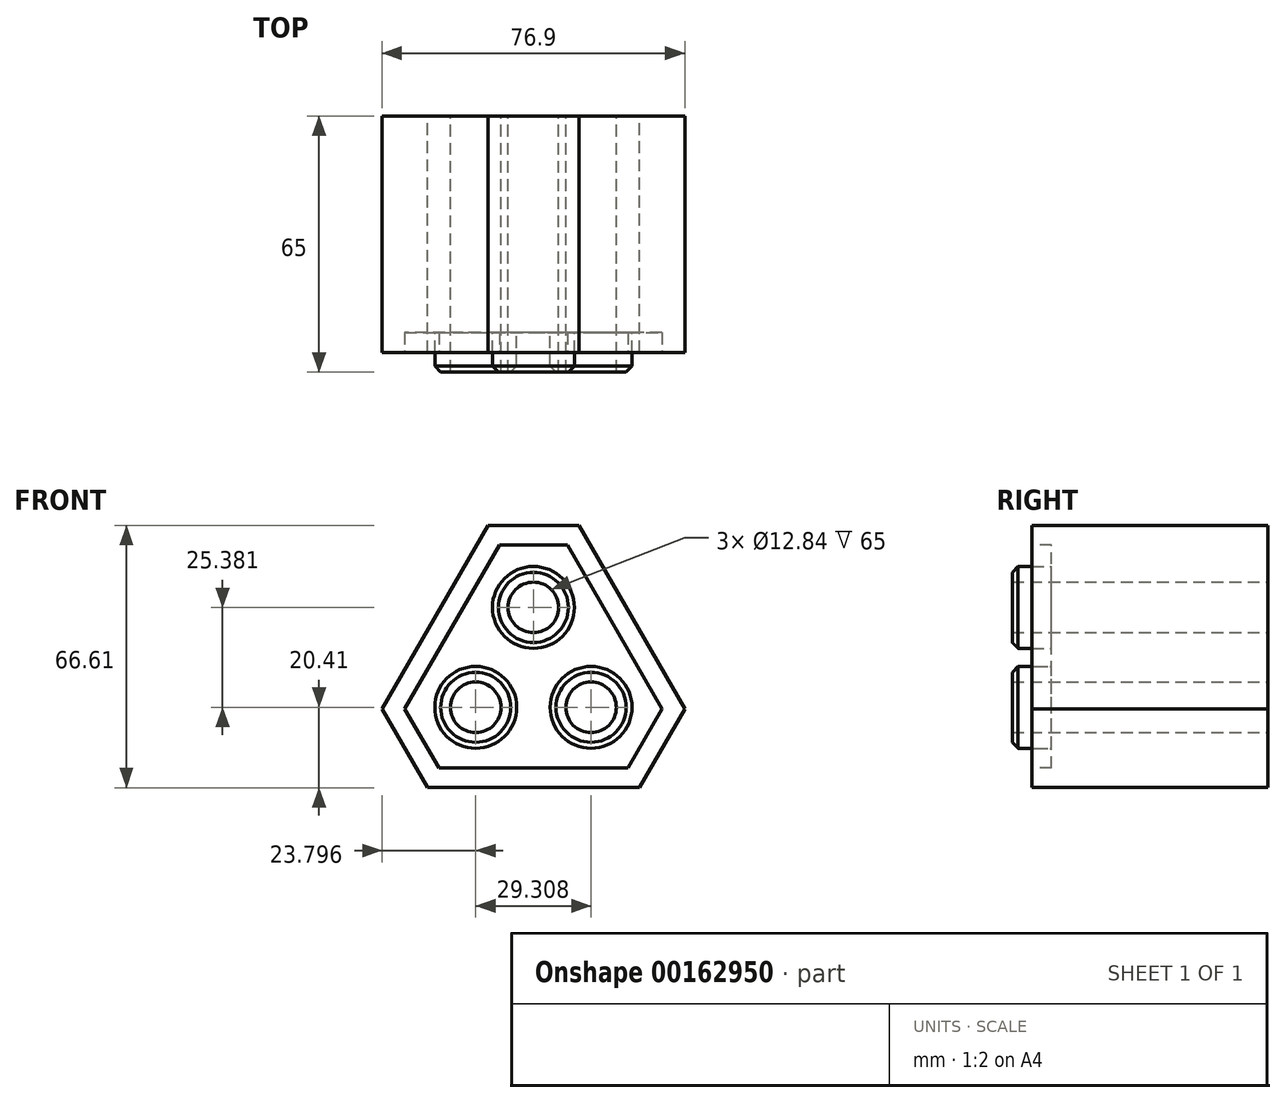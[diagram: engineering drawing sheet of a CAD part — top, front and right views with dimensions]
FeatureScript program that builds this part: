
annotation { "Feature Type Name" : "Feature", "Feature Type Description" : "" }
export const myFeature = defineFeature(function(context is Context, id is Id, definition is map)
    precondition{}
    {
        {
            assignVariable(context, id + "F0", {"name" : "loop", "anyValue" : 60});
        }
        {
            var Q0;
            Q0=qCreatedBy(makeId("Front.planeOp"),FACE);
            var sketch = newSketch(context, id + "F1", { "sketchPlane" : qUnion([Q0])});
            skCircle(sketch, "E0.cCircle", {"center": v(0, 0) * mm, "radius": 28.87 * mm, "construction": true});
            skLineSegment(sketch, "E0.0", {"start": v(50, -28.87) * mm, "end": v(-50, -28.87) * mm});
            skLineSegment(sketch, "E0.1", {"start": v(-50, -28.87) * mm, "end": v(0, 57.74) * mm});
            skLineSegment(sketch, "E0.2", {"start": v(0, 57.74) * mm, "end": v(50, -28.87) * mm});
            skPoint(sketch, "E0.0.midPoint", {"position": v(0, -28.87) * mm});
            skLineSegment(sketch, "E1", {"start": v(-11.55, 37.74) * mm, "end": v(11.55, 37.74) * mm});
            skLineSegment(sketch, "E2.1.0", {"start": v(-26.9, -28.87) * mm, "end": v(-38.45, -8.87) * mm});
            skLineSegment(sketch, "E2.2.0", {"start": v(38.45, -8.87) * mm, "end": v(26.9, -28.87) * mm});
            skSolve(sketch);
        }
        {
            var Q0;
            {var subQ0=sQuery(id+"F1.wireOp",EDGE,"E1");Q0=makeQuery(id+"F1.imprint","IMPRINT",FACE,{"disambiguationData":[TD([[makeQuery(id+"F1.imprint","IMPRINT",EDGE,{"derivedFrom":subQ0}),-1.0]])]});}
            extrude(context, id + "F2", {"entities" : qUnion([Q0]), "depth" : (getVariable(context, 'loop')) * mm, "offsetDistance" : 25 * mm});
        }
        {
            var Q0;
            Q0=makeQuery(id+"F2.opExtrude","CAP_FACE",FACE,{"disambiguationData":[OSD([sQuery(id+"F1.wireOp",EDGE,"E0.0"),sQuery(id+"F1.wireOp",EDGE,"E0.1"),sQuery(id+"F1.wireOp",EDGE,"E0.2"),sQuery(id+"F1.wireOp",EDGE,"E1"),sQuery(id+"F1.wireOp",EDGE,"E2.1.0"),sQuery(id+"F1.wireOp",EDGE,"E2.2.0")])],"isStart":false});
            var sketch = newSketch(context, id + "F3", { "sketchPlane" : qUnion([Q0])});
            skLineSegment(sketch, "E3.0", {"start": v(-24.02, -23.87) * mm, "end": v(24.02, -23.87) * mm});
            skLineSegment(sketch, "E3.1", {"start": v(32.68, -8.87) * mm, "end": v(8.66, 32.74) * mm});
            skLineSegment(sketch, "E3.2", {"start": v(8.66, 32.74) * mm, "end": v(-8.66, 32.74) * mm});
            skLineSegment(sketch, "E3.3", {"start": v(24.02, -23.87) * mm, "end": v(32.68, -8.87) * mm});
            skLineSegment(sketch, "E3.4", {"start": v(-8.66, 32.74) * mm, "end": v(-32.68, -8.87) * mm});
            skLineSegment(sketch, "E3.5", {"start": v(-32.68, -8.87) * mm, "end": v(-24.02, -23.87) * mm});
            skSolve(sketch);
        }
        {
            var Q0;
            Q0=makeQuery(id+"F3.imprint","IMPRINT",FACE,{"disambiguationData":[TD([[makeQuery(id+"F3.imprint","IMPRINT",EDGE,{"derivedFrom":sQuery(id+"F3.wireOp",EDGE,"E3.0")}),1.0]])]});
            extrude(context, id + "F4", {"entities" : qUnion([Q0]), "operationType" : NewBodyOperationType.REMOVE, "oppositeDirection" : true, "depth" : 5 * mm, "offsetDistance" : 25 * mm});
        }
        {
            var Q0;
            Q0=makeQuery(id+"F4.boolean.opBoolean","COPY",FACE,{"derivedFrom":makeQuery(id+"F4.opExtrude","CAP_FACE",FACE,{"disambiguationData":[OSD([sQuery(id+"F3.wireOp",EDGE,"E3.0"),sQuery(id+"F3.wireOp",EDGE,"E3.1"),sQuery(id+"F3.wireOp",EDGE,"E3.2"),sQuery(id+"F3.wireOp",EDGE,"E3.3"),sQuery(id+"F3.wireOp",EDGE,"E3.4"),sQuery(id+"F3.wireOp",EDGE,"E3.5")])],"isStart":false})});
            var sketch = newSketch(context, id + "F5", { "sketchPlane" : qUnion([Q0])});
            skCircle(sketch, "E4", {"center": v(0, 16.92) * mm, "radius": 10.4 * mm});
            skCircle(sketch, "E5", {"center": v(0, 16.92) * mm, "radius": 6.42 * mm});
            skCircle(sketch, "E6.1.0", {"center": v(-14.65, -8.46) * mm, "radius": 10.4 * mm});
            skCircle(sketch, "E6.1.1", {"center": v(-14.65, -8.46) * mm, "radius": 6.42 * mm});
            skCircle(sketch, "E6.2.0", {"center": v(14.65, -8.46) * mm, "radius": 10.4 * mm});
            skCircle(sketch, "E6.2.1", {"center": v(14.65, -8.46) * mm, "radius": 6.42 * mm});
            skPoint(sketch, "E6.center", {"position": v(0, 0) * mm});
            skSolve(sketch);
        }
        {
            var Q0;
            Q0 = qSketchRegion(id + "F5", true);
            var Q1;
            Q1 = qConstructionFilter(qBodyType(qCreatedBy(id + "F5" ,EDGE), BodyType.WIRE), ConstructionObject.NO);
            extrude(context, id + "F6", {"entities" : qUnion([Q0]), "operationType" : NewBodyOperationType.ADD, "surfaceEntities" : qUnion([Q1]), "depth" : 10 * mm, "offsetDistance" : 25 * mm});
        }
        {
            var Q0;
            Q0=makeQuery(id+"F6.opExtrude","CAP_EDGE",EDGE,{"disambiguationData":[OSD([sQuery(id+"F5.wireOp",EDGE,"E4")])],"isStart":false});
            var Q1;
            Q1=makeQuery(id+"F6.opExtrude","CAP_EDGE",EDGE,{"disambiguationData":[OSD([sQuery(id+"F5.wireOp",EDGE,"E6.1.0")])],"isStart":false});
            var Q2;
            Q2=makeQuery(id+"F6.opExtrude","CAP_EDGE",EDGE,{"disambiguationData":[OSD([sQuery(id+"F5.wireOp",EDGE,"E6.2.0")])],"isStart":false});
            chamfer(context, id + "F7", {"entities" : qUnion([Q0, Q1, Q2]), "width" : 1.5 * mm, "tangentPropagation" : true});
        }
        {
            var Q0;
            Q0=makeQuery(id+"F6.boolean.opBoolean","SPLIT",FACE,{"disambiguationData":[TD([makeQuery(id+"F6.opExtrude","SWEPT_FACE",FACE,{"disambiguationData":[OSD([sQuery(id+"F5.wireOp",EDGE,"E5")])]})])],"derivedFrom":makeQuery(id+"F4.boolean.opBoolean","COPY",FACE,{"derivedFrom":makeQuery(id+"F4.opExtrude","CAP_FACE",FACE,{"disambiguationData":[OSD([sQuery(id+"F3.wireOp",EDGE,"E3.0"),sQuery(id+"F3.wireOp",EDGE,"E3.1"),sQuery(id+"F3.wireOp",EDGE,"E3.2"),sQuery(id+"F3.wireOp",EDGE,"E3.3"),sQuery(id+"F3.wireOp",EDGE,"E3.4"),sQuery(id+"F3.wireOp",EDGE,"E3.5")])],"isStart":false})})});
            var Q1;
            Q1=makeQuery(id+"F6.boolean.opBoolean","SPLIT",FACE,{"disambiguationData":[TD([makeQuery(id+"F6.opExtrude","SWEPT_FACE",FACE,{"disambiguationData":[OSD([sQuery(id+"F5.wireOp",EDGE,"E6.1.1")])]})])],"derivedFrom":makeQuery(id+"F4.boolean.opBoolean","COPY",FACE,{"derivedFrom":makeQuery(id+"F4.opExtrude","CAP_FACE",FACE,{"disambiguationData":[OSD([sQuery(id+"F3.wireOp",EDGE,"E3.0"),sQuery(id+"F3.wireOp",EDGE,"E3.1"),sQuery(id+"F3.wireOp",EDGE,"E3.2"),sQuery(id+"F3.wireOp",EDGE,"E3.3"),sQuery(id+"F3.wireOp",EDGE,"E3.4"),sQuery(id+"F3.wireOp",EDGE,"E3.5")])],"isStart":false})})});
            var Q2;
            Q2=makeQuery(id+"F6.boolean.opBoolean","SPLIT",FACE,{"disambiguationData":[TD([makeQuery(id+"F6.opExtrude","SWEPT_FACE",FACE,{"disambiguationData":[OSD([sQuery(id+"F5.wireOp",EDGE,"E6.2.1")])]})])],"derivedFrom":makeQuery(id+"F4.boolean.opBoolean","COPY",FACE,{"derivedFrom":makeQuery(id+"F4.opExtrude","CAP_FACE",FACE,{"disambiguationData":[OSD([sQuery(id+"F3.wireOp",EDGE,"E3.0"),sQuery(id+"F3.wireOp",EDGE,"E3.1"),sQuery(id+"F3.wireOp",EDGE,"E3.2"),sQuery(id+"F3.wireOp",EDGE,"E3.3"),sQuery(id+"F3.wireOp",EDGE,"E3.4"),sQuery(id+"F3.wireOp",EDGE,"E3.5")])],"isStart":false})})});
            extrude(context, id + "F8", {"entities" : qUnion([Q0, Q1, Q2]), "operationType" : NewBodyOperationType.REMOVE, "oppositeDirection" : true, "depth" : 300 * mm, "offsetDistance" : 25 * mm});
        }
    });
